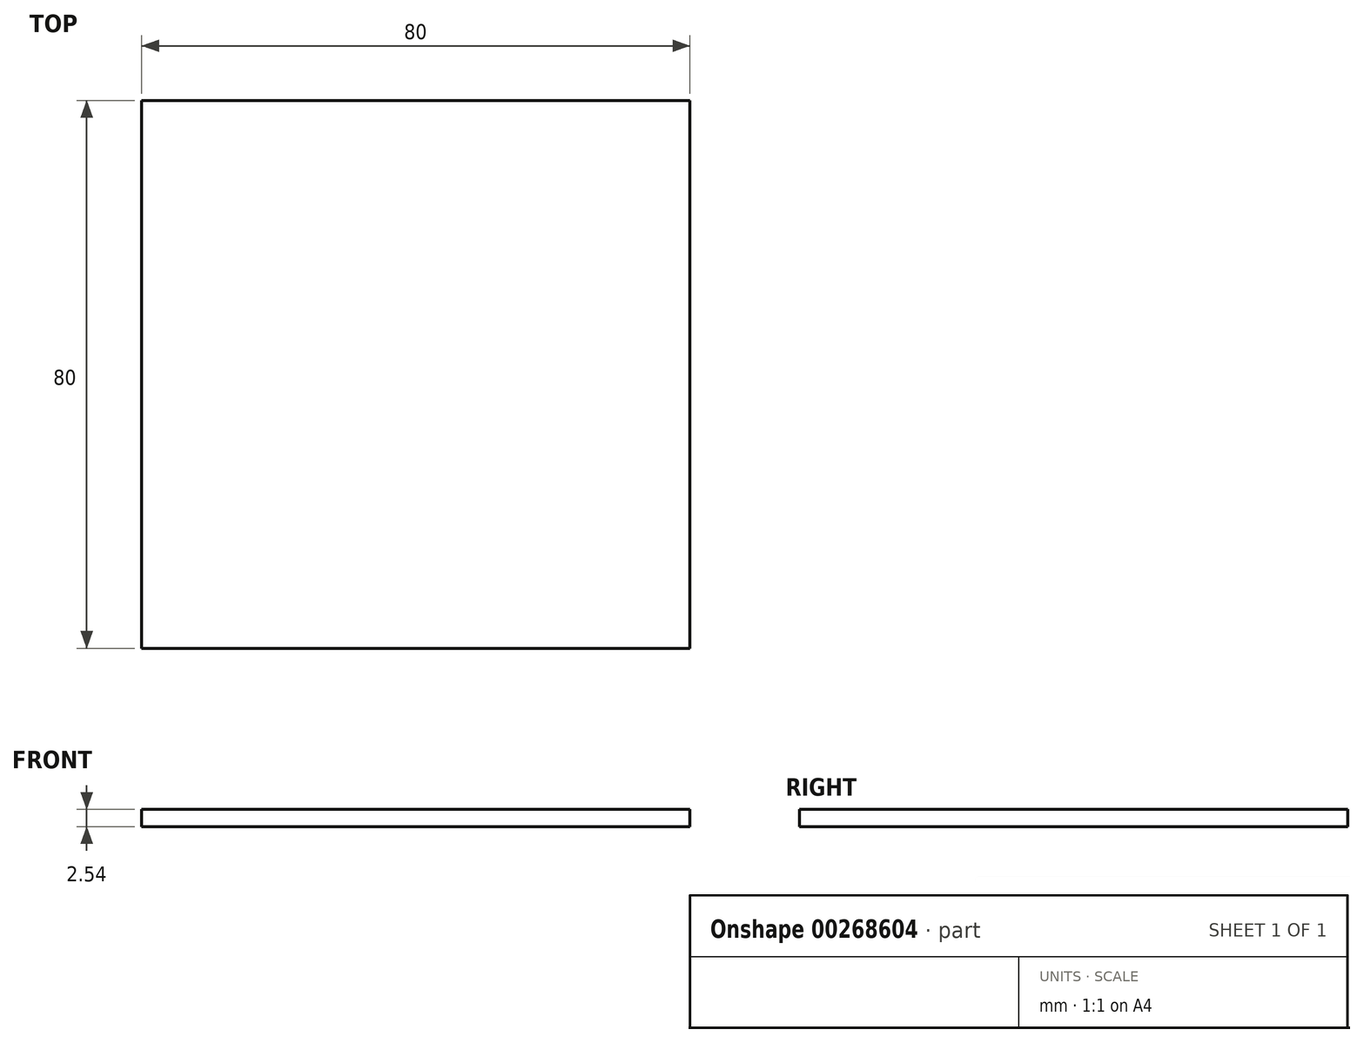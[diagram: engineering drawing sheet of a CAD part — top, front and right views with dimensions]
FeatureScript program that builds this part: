
annotation { "Feature Type Name" : "Feature", "Feature Type Description" : "" }
export const myFeature = defineFeature(function(context is Context, id is Id, definition is map)
    precondition{}
    {
        {
            var Q0;
            Q0=qCreatedBy(makeId("Top.planeOp"),FACE);
            var sketch = newSketch(context, id + "F0", { "sketchPlane" : qUnion([Q0])});
            skLineSegment(sketch, "E0.bottom", {"start": v(40, -40) * mm, "end": v(-40, -40) * mm});
            skLineSegment(sketch, "E0.top", {"start": v(40, 40) * mm, "end": v(-40, 40) * mm});
            skLineSegment(sketch, "E0.left", {"start": v(40, -40) * mm, "end": v(40, 40) * mm});
            skLineSegment(sketch, "E0.right", {"start": v(-40, -40) * mm, "end": v(-40, 40) * mm});
            skPoint(sketch, "E0.middle", {"position": v(0, 0) * mm});
            skSolve(sketch);
        }
        {
            var Q0;
            Q0=makeQuery(id+"F0.imprint","IMPRINT",FACE,{"disambiguationData":[TD([[makeQuery(id+"F0.imprint","IMPRINT",EDGE,{"derivedFrom":sQuery(id+"F0.wireOp",EDGE,"E0.bottom")}),-1.0]])]});
            extrude(context, id + "F1", {"entities" : qUnion([Q0]), "depth" : 2.54 * mm});
        }
    });
